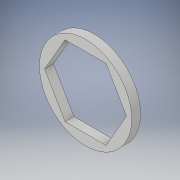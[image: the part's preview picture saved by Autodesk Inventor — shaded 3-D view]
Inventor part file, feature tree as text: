
AUTODESK INVENTOR PART (.ipt)
format: ipt  version: 2018 (Build 220112000, 112)  size: 103,936 bytes
history: native  units: in
note: dims shown in document units (in); Inventor stores cm internally (conversion verified against a paired STEP export)
features: extrude x1, sketch x1
ambient origin geometry x8: Origin, YZ Plane, XZ Plane, XY Plane, X Axis, Y Axis, Z Axis, Center Point
bodies: Solid1 (feature_tree)
feature tree (2):
  extrude  "Extrusion1"  Depth=0.0625in
  sketch  "Sketch1"  dims[d0=0.5in d1=0.65in d2=0.0625in d3=0.0in]
